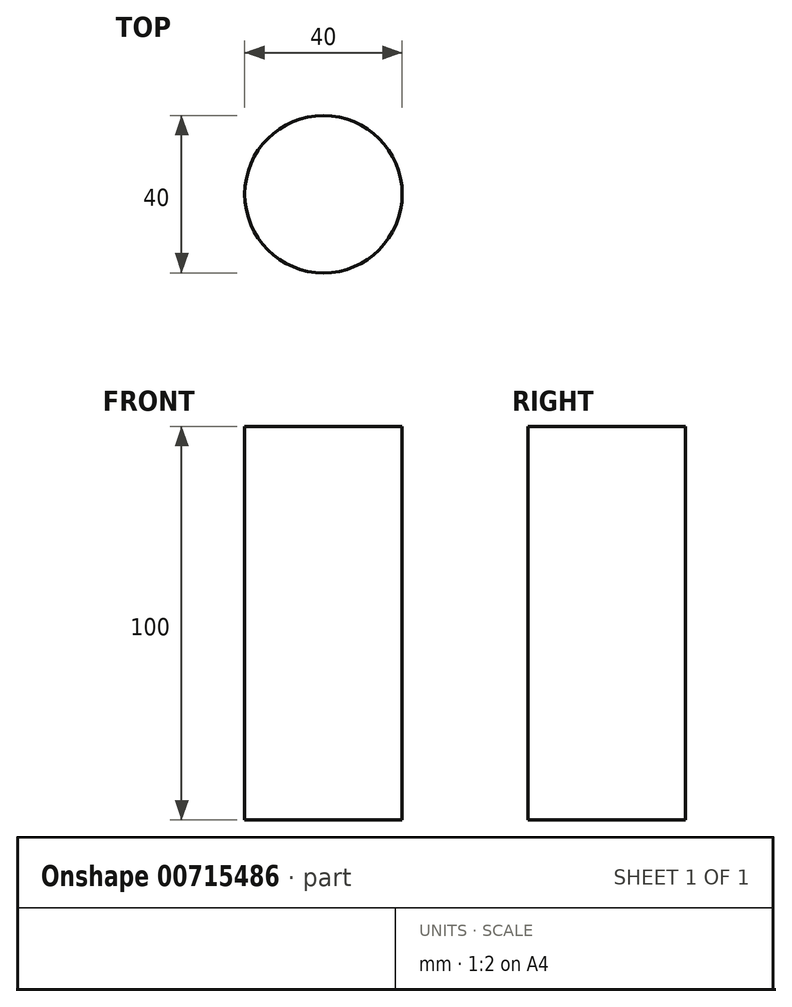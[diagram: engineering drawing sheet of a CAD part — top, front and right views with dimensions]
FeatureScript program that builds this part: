
annotation { "Feature Type Name" : "Feature", "Feature Type Description" : "" }
export const myFeature = defineFeature(function(context is Context, id is Id, definition is map)
    precondition{}
    {
        {
            var Q0;
            Q0=qCreatedBy(makeId("Top.planeOp"),FACE);
            var sketch = newSketch(context, id + "F0", { "sketchPlane" : qUnion([Q0])});
            skCircle(sketch, "E0", {"center": v(0, 0) * mm, "radius": 20 * mm});
            skSolve(sketch);
        }
        {
            var Q0;
            Q0 = qSketchRegion(id + "F0", true);
            extrude(context, id + "F1", {"entities" : qUnion([Q0]), "flatOperationType" : FlatOperationType.REMOVE, "depth" : 100 * mm, "offsetDistance" : 25.4 * mm, "domain" : OperationDomain.MODEL, "symmetric" : true});
        }
    });
